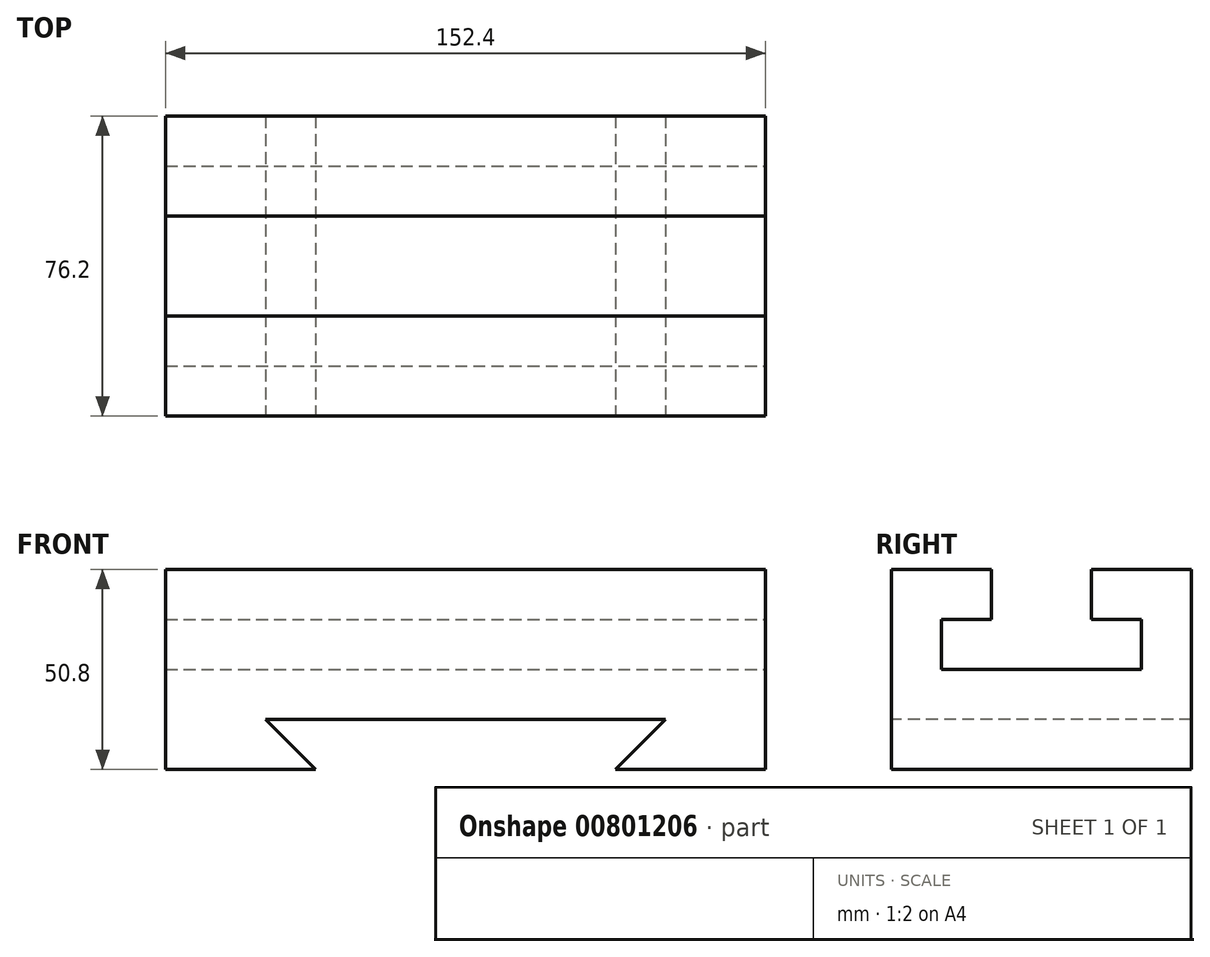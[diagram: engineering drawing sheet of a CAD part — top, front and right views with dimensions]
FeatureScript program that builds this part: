
annotation { "Feature Type Name" : "Feature", "Feature Type Description" : "" }
export const myFeature = defineFeature(function(context is Context, id is Id, definition is map)
    precondition{}
    {
        {
            var Q0;
            Q0=qCreatedBy(makeId("Right.planeOp"),FACE);
            var sketch = newSketch(context, id + "F0", { "sketchPlane" : qUnion([Q0])});
            skLineSegment(sketch, "E0.bottom", {"start": v(-76.2, -21.29) * mm, "end": v(0, -21.29) * mm});
            skLineSegment(sketch, "E0.top", {"start": v(-76.2, 4.11) * mm, "end": v(0, 4.11) * mm});
            skLineSegment(sketch, "E0.left", {"start": v(-76.2, -21.29) * mm, "end": v(-76.2, 4.11) * mm});
            skLineSegment(sketch, "E0.right", {"start": v(0, -21.29) * mm, "end": v(0, 4.11) * mm});
            skLineSegment(sketch, "E1.bottom", {"start": v(-76.2, 16.81) * mm, "end": v(-63.5, 16.81) * mm});
            skLineSegment(sketch, "E1.top", {"start": v(-76.2, 4.11) * mm, "end": v(-63.5, 4.11) * mm});
            skLineSegment(sketch, "E1.left", {"start": v(-76.2, 16.81) * mm, "end": v(-76.2, 4.11) * mm});
            skLineSegment(sketch, "E1.right", {"start": v(-63.5, 16.81) * mm, "end": v(-63.5, 4.11) * mm});
            skLineSegment(sketch, "E2.top", {"start": v(-12.7, 4.11) * mm, "end": v(0, 4.11) * mm});
            skLineSegment(sketch, "E2.left", {"start": v(-12.7, 16.81) * mm, "end": v(-12.7, 4.11) * mm});
            skLineSegment(sketch, "E2.right", {"start": v(0, 16.81) * mm, "end": v(0, 4.11) * mm});
            skLineSegment(sketch, "E3.bottom", {"start": v(-76.2, 29.51) * mm, "end": v(-50.8, 29.51) * mm});
            skLineSegment(sketch, "E3.top", {"start": v(-76.2, 16.81) * mm, "end": v(-50.8, 16.81) * mm});
            skLineSegment(sketch, "E3.left", {"start": v(-76.2, 29.51) * mm, "end": v(-76.2, 16.81) * mm});
            skLineSegment(sketch, "E3.right", {"start": v(-50.8, 29.51) * mm, "end": v(-50.8, 16.81) * mm});
            skLineSegment(sketch, "E4.bottom", {"start": v(-25.4, 29.51) * mm, "end": v(0, 29.51) * mm});
            skLineSegment(sketch, "E4.top", {"start": v(-25.4, 16.81) * mm, "end": v(0, 16.81) * mm});
            skLineSegment(sketch, "E4.left", {"start": v(-25.4, 29.51) * mm, "end": v(-25.4, 16.81) * mm});
            skLineSegment(sketch, "E4.right", {"start": v(0, 29.51) * mm, "end": v(0, 16.81) * mm});
            skSolve(sketch);
        }
        {
            var Q0;
            Q0=makeQuery(id+"F0.imprint","IMPRINT",FACE,{"disambiguationData":[TD([[makeQuery(id+"F0.imprint","IMPRINT",EDGE,{"derivedFrom":sQuery(id+"F0.wireOp",EDGE,"E0.bottom")}),1.0]])]});
            var Q1;
            Q1=makeQuery(id+"F0.imprint","IMPRINT",FACE,{"disambiguationData":[TD([[makeQuery(id+"F0.imprint","IMPRINT",EDGE,{"derivedFrom":sQuery(id+"F0.wireOp",EDGE,"E1.bottom")}),-1.0]])]});
            var Q2;
            Q2=makeQuery(id+"F0.imprint","IMPRINT",FACE,{"disambiguationData":[TD([[makeQuery(id+"F0.imprint","IMPRINT",EDGE,{"derivedFrom":sQuery(id+"F0.wireOp",EDGE,"E1.bottom")}),1.0]])]});
            var Q3;
            Q3=makeQuery(id+"F0.imprint","IMPRINT",FACE,{"disambiguationData":[TD([[makeQuery(id+"F0.imprint","IMPRINT",EDGE,{"derivedFrom":sQuery(id+"F0.wireOp",EDGE,"E4.bottom")}),-1.0]])]});
            var Q4;
            {var subQ2=sQuery(id+"F0.wireOp",EDGE,"E2.left");Q4=makeQuery(id+"F0.imprint","IMPRINT",FACE,{"disambiguationData":[TD([[makeQuery(id+"F0.imprint","IMPRINT",EDGE,{"derivedFrom":subQ2}),1.0]])]});}
            extrude(context, id + "F1", {"entities" : qUnion([Q0, Q1, Q2, Q3, Q4]), "depth" : -152.4 * mm, "offsetDistance" : 25.4 * mm});
        }
        {
            var Q0;
            Q0=makeQuery(id+"F1.opExtrude","SWEPT_FACE",FACE,{"disambiguationData":[OSD([sQuery(id+"F0.wireOp",EDGE,"E0.left"),sQuery(id+"F0.wireOp",EDGE,"E1.left"),sQuery(id+"F0.wireOp",EDGE,"E3.left")])]});
            var sketch = newSketch(context, id + "F2", { "sketchPlane" : qUnion([Q0])});
            skLineSegment(sketch, "E5", {"start": v(-114.3, -21.29) * mm, "end": v(-127, -8.59) * mm});
            skLineSegment(sketch, "E6", {"start": v(-127, -8.59) * mm, "end": v(-25.4, -8.59) * mm});
            skLineSegment(sketch, "E7", {"start": v(-25.4, -8.59) * mm, "end": v(-38.1, -21.29) * mm});
            skSolve(sketch);
        }
        {
            var Q0;
            {var subQ0=sQuery(id+"F2.wireOp",EDGE,"E5");Q0=makeQuery(id+"F2.imprint","IMPRINT",FACE,{"disambiguationData":[TD([[makeQuery(id+"F2.imprint","IMPRINT",EDGE,{"derivedFrom":subQ0}),-1.0]])]});}
            extrude(context, id + "F3", {"entities" : qUnion([Q0]), "operationType" : NewBodyOperationType.REMOVE, "endBound" : BoundingType.THROUGH_ALL, "oppositeDirection" : true, "depth" : 25.4 * mm, "offsetDistance" : 25.4 * mm});
        }
    });
